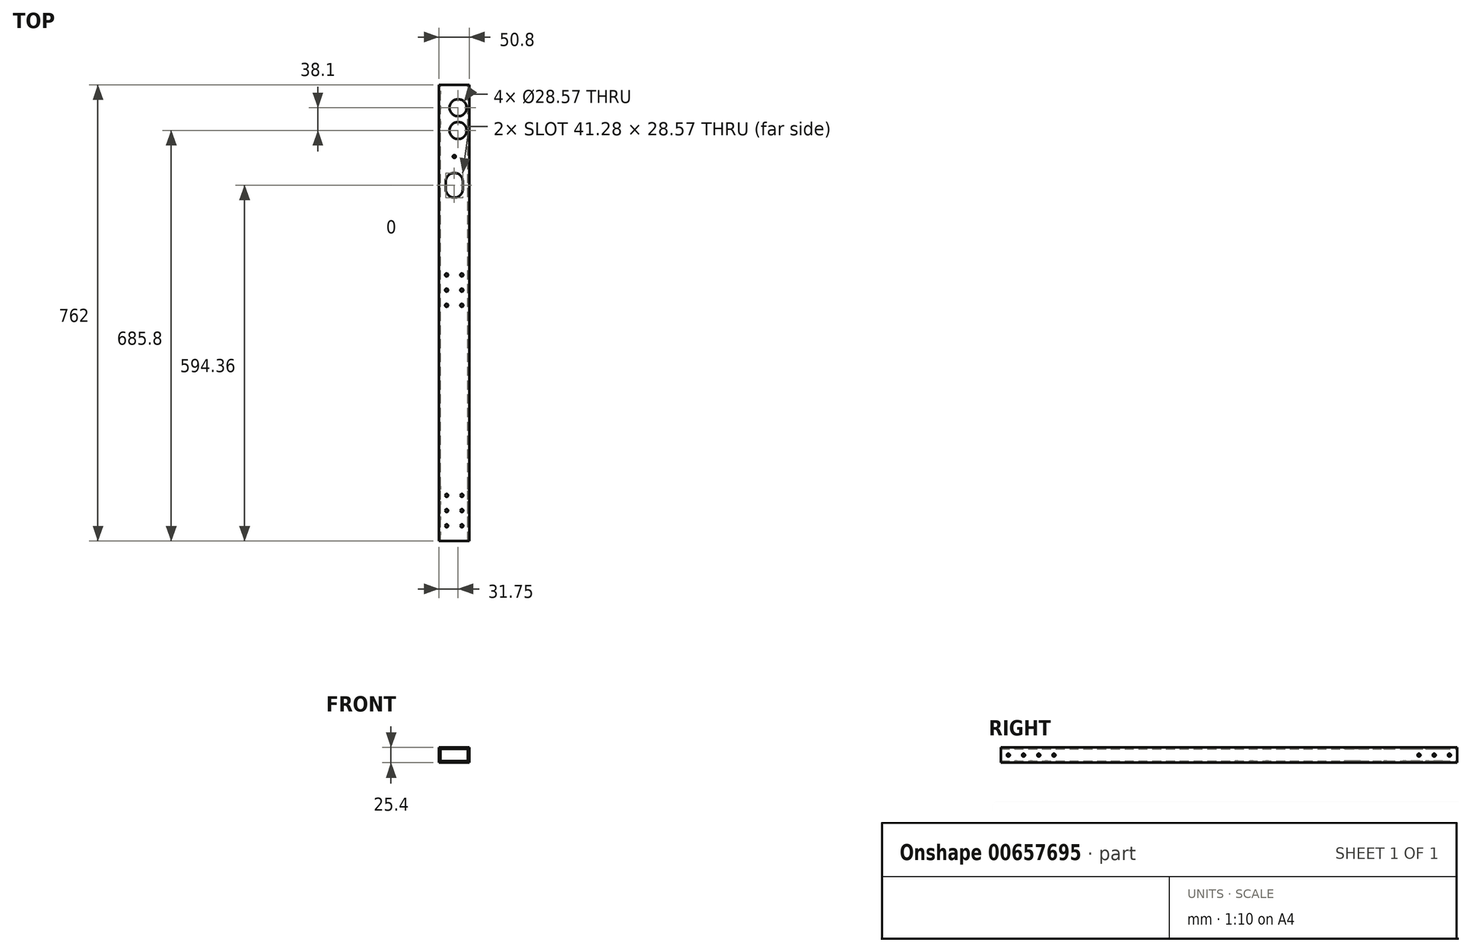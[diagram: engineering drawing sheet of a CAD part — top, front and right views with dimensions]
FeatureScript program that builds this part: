
annotation { "Feature Type Name" : "Feature", "Feature Type Description" : "" }
export const myFeature = defineFeature(function(context is Context, id is Id, definition is map)
    precondition{}
    {
        {
            var Q0;
            Q0=qCreatedBy(makeId("Front.planeOp"),FACE);
            var sketch = newSketch(context, id + "F0", { "sketchPlane" : qUnion([Q0])});
            skLineSegment(sketch, "E0.bottom", {"start": v(0, 0) * mm, "end": v(50.8, 0) * mm});
            skLineSegment(sketch, "E0.top", {"start": v(0, 25.4) * mm, "end": v(50.8, 25.4) * mm});
            skLineSegment(sketch, "E0.left", {"start": v(0, 0) * mm, "end": v(0, 25.4) * mm});
            skLineSegment(sketch, "E0.right", {"start": v(50.8, 0) * mm, "end": v(50.8, 25.4) * mm});
            skLineSegment(sketch, "E1.bottom", {"start": v(2.54, 22.86) * mm, "end": v(48.26, 22.86) * mm});
            skLineSegment(sketch, "E1.top", {"start": v(2.54, 2.54) * mm, "end": v(48.26, 2.54) * mm});
            skLineSegment(sketch, "E1.left", {"start": v(2.54, 22.86) * mm, "end": v(2.54, 2.54) * mm});
            skLineSegment(sketch, "E1.right", {"start": v(48.26, 22.86) * mm, "end": v(48.26, 2.54) * mm});
            skSolve(sketch);
        }
        {
            var Q0;
            Q0=makeQuery(id+"F0.imprint","IMPRINT",FACE,{"disambiguationData":[TD([[makeQuery(id+"F0.imprint","IMPRINT",EDGE,{"derivedFrom":sQuery(id+"F0.wireOp",EDGE,"E0.bottom")}),1.0]])]});
            extrude(context, id + "F1", {"entities" : qUnion([Q0]), "depth" : 787.4 * mm, "offsetDistance" : 25.4 * mm});
        }
        {
            var Q0;
            Q0=makeQuery(id+"F1.opExtrude","SWEPT_FACE",FACE,{"disambiguationData":[OSD([sQuery(id+"F0.wireOp",EDGE,"E0.right")])]});
            var sketch = newSketch(context, id + "F2", { "sketchPlane" : qUnion([Q0])});
            skLineSegment(sketch, "E2", {"start": v(0, 12.7) * mm, "end": v(-787.4, 12.7) * mm, "construction": true});
            skCircle(sketch, "E3", {"center": v(-12.7, 12.7) * mm, "radius": 2.55 * mm});
            skCircle(sketch, "E4", {"center": v(-38.1, 12.7) * mm, "radius": 2.55 * mm});
            skCircle(sketch, "E5", {"center": v(-63.5, 12.7) * mm, "radius": 2.55 * mm});
            skCircle(sketch, "E6", {"center": v(-88.9, 12.7) * mm, "radius": 2.55 * mm});
            skCircle(sketch, "E7", {"center": v(-774.7, 12.7) * mm, "radius": 2.55 * mm});
            skCircle(sketch, "E8", {"center": v(-749.3, 12.7) * mm, "radius": 2.55 * mm});
            skCircle(sketch, "E9", {"center": v(-723.9, 12.7) * mm, "radius": 2.55 * mm});
            skCircle(sketch, "E10", {"center": v(-698.5, 12.7) * mm, "radius": 2.55 * mm});
            skSolve(sketch);
        }
        {
            var Q0;
            Q0=makeQuery(id+"F1.opExtrude","SWEPT_FACE",FACE,{"disambiguationData":[OSD([sQuery(id+"F0.wireOp",EDGE,"E0.top")])]});
            var sketch = newSketch(context, id + "F3", { "sketchPlane" : qUnion([Q0])});
            skCircle(sketch, "E11", {"center": v(31.75, -63.5) * mm, "radius": 14.29 * mm});
            skCircle(sketch, "E12", {"center": v(25.4, -186.7) * mm, "radius": 14.29 * mm});
            skCircle(sketch, "E13", {"center": v(25.4, -199.39) * mm, "radius": 14.29 * mm});
            skCircle(sketch, "E14", {"center": v(12.7, -736.6) * mm, "radius": 2.49 * mm});
            skCircle(sketch, "E15.0.1.0", {"center": v(12.7, -711.2) * mm, "radius": 2.49 * mm});
            skCircle(sketch, "E15.1.0.0", {"center": v(38.1, -736.6) * mm, "radius": 2.49 * mm});
            skCircle(sketch, "E15.1.1.0", {"center": v(38.1, -711.2) * mm, "radius": 2.49 * mm});
            skLineSegment(sketch, "E15.direction1", {"start": v(12.7, -736.6) * mm, "end": v(38.1, -736.6) * mm, "construction": true});
            skLineSegment(sketch, "E15.direction2", {"start": v(12.7, -736.6) * mm, "end": v(12.7, -711.2) * mm, "construction": true});
            skCircle(sketch, "E16", {"center": v(12.7, -342.9) * mm, "radius": 2.55 * mm});
            skPoint(sketch, "E17", {"position": v(0, -341.39) * mm});
            skCircle(sketch, "E18.0.1.0", {"center": v(12.7, -368.3) * mm, "radius": 2.55 * mm});
            skCircle(sketch, "E18.0.2.0", {"center": v(12.7, -393.7) * mm, "radius": 2.55 * mm});
            skCircle(sketch, "E18.1.0.0", {"center": v(38.1, -342.9) * mm, "radius": 2.55 * mm});
            skCircle(sketch, "E18.1.1.0", {"center": v(38.1, -368.3) * mm, "radius": 2.55 * mm});
            skCircle(sketch, "E18.1.2.0", {"center": v(38.1, -393.7) * mm, "radius": 2.55 * mm});
            skLineSegment(sketch, "E18.direction1", {"start": v(12.7, -342.9) * mm, "end": v(38.1, -342.9) * mm, "construction": true});
            skLineSegment(sketch, "E18.direction2", {"start": v(12.7, -342.9) * mm, "end": v(12.7, -368.3) * mm, "construction": true});
            skLineSegment(sketch, "E19", {"start": v(39.69, -186.7) * mm, "end": v(39.69, -199.39) * mm});
            skLineSegment(sketch, "E20", {"start": v(11.11, -186.7) * mm, "end": v(11.11, -199.39) * mm});
            skCircle(sketch, "E21", {"center": v(25.4, -145.03) * mm, "radius": 2.49 * mm});
            skCircle(sketch, "E22", {"center": v(38.1, -762) * mm, "radius": 2.49 * mm});
            skCircle(sketch, "E23", {"center": v(12.7, -762) * mm, "radius": 2.49 * mm});
            skLineSegment(sketch, "E24.bottom", {"start": v(0, 0) * mm, "end": v(50.8, 0) * mm});
            skLineSegment(sketch, "E24.top", {"start": v(0, -25.4) * mm, "end": v(50.8, -25.4) * mm});
            skLineSegment(sketch, "E24.left", {"start": v(0, 0) * mm, "end": v(0, -25.4) * mm});
            skLineSegment(sketch, "E24.right", {"start": v(50.8, 0) * mm, "end": v(50.8, -25.4) * mm});
            skCircle(sketch, "E25", {"center": v(31.75, -101.6) * mm, "radius": 14.29 * mm});
            skSolve(sketch);
        }
        {
            var Q0;
            Q0=makeQuery(id+"F3.imprint","IMPRINT",FACE,{"disambiguationData":[TD([[makeQuery(id+"F3.imprint","IMPRINT",EDGE,{"derivedFrom":sQuery(id+"F3.wireOp",EDGE,"E11")}),1.0]])]});
            var Q1;
            Q1=makeQuery(id+"F3.imprint","IMPRINT",FACE,{"disambiguationData":[TD([[makeQuery(id+"F3.imprint","IMPRINT",EDGE,{"derivedFrom":sQuery(id+"F3.wireOp",EDGE,"uvUDpf29-BH4l-E19a-3uxY-FCehscGXEqBA")}),1.0]])]});
            var Q2;
            Q2=makeQuery(id+"F3.imprint","IMPRINT",FACE,{"disambiguationData":[TD([[makeQuery(id+"F3.imprint","IMPRINT",EDGE,{"derivedFrom":sQuery(id+"F3.wireOp",EDGE,"E14")}),1.0]])]});
            var Q3;
            Q3=makeQuery(id+"F3.imprint","IMPRINT",FACE,{"disambiguationData":[TD([[makeQuery(id+"F3.imprint","IMPRINT",EDGE,{"derivedFrom":sQuery(id+"F3.wireOp",EDGE,"E15.1.0.0")}),1.0]])]});
            var Q4;
            Q4=makeQuery(id+"F3.imprint","IMPRINT",FACE,{"disambiguationData":[TD([[makeQuery(id+"F3.imprint","IMPRINT",EDGE,{"derivedFrom":sQuery(id+"F3.wireOp",EDGE,"E15.0.1.0")}),1.0]])]});
            var Q5;
            Q5=makeQuery(id+"F3.imprint","IMPRINT",FACE,{"disambiguationData":[TD([[makeQuery(id+"F3.imprint","IMPRINT",EDGE,{"derivedFrom":sQuery(id+"F3.wireOp",EDGE,"E15.1.1.0")}),1.0]])]});
            var Q6;
            Q6=makeQuery(id+"F3.imprint","IMPRINT",FACE,{"disambiguationData":[TD([[makeQuery(id+"F3.imprint","IMPRINT",EDGE,{"derivedFrom":sQuery(id+"F3.wireOp",EDGE,"E18.1.2.0")}),1.0]])]});
            var Q7;
            Q7=makeQuery(id+"F3.imprint","IMPRINT",FACE,{"disambiguationData":[TD([[makeQuery(id+"F3.imprint","IMPRINT",EDGE,{"derivedFrom":sQuery(id+"F3.wireOp",EDGE,"E18.1.1.0")}),1.0]])]});
            var Q8;
            Q8=makeQuery(id+"F3.imprint","IMPRINT",FACE,{"disambiguationData":[TD([[makeQuery(id+"F3.imprint","IMPRINT",EDGE,{"derivedFrom":sQuery(id+"F3.wireOp",EDGE,"E16")}),1.0]])]});
            var Q9;
            Q9=makeQuery(id+"F3.imprint","IMPRINT",FACE,{"disambiguationData":[TD([[makeQuery(id+"F3.imprint","IMPRINT",EDGE,{"derivedFrom":sQuery(id+"F3.wireOp",EDGE,"E18.1.0.0")}),1.0]])]});
            var Q10;
            Q10=makeQuery(id+"F3.imprint","IMPRINT",FACE,{"disambiguationData":[TD([[makeQuery(id+"F3.imprint","IMPRINT",EDGE,{"derivedFrom":sQuery(id+"F3.wireOp",EDGE,"E18.0.1.0")}),1.0]])]});
            var Q11;
            Q11=makeQuery(id+"F3.imprint","IMPRINT",FACE,{"disambiguationData":[TD([[makeQuery(id+"F3.imprint","IMPRINT",EDGE,{"derivedFrom":sQuery(id+"F3.wireOp",EDGE,"E18.0.2.0")}),1.0]])]});
            var Q12;
            {var subQ0=sQuery(id+"F3.wireOp",EDGE,"E12");var subQ1=makeQuery(id+"F3.imprint","INTERSECT",VERTEX,{"derivedFrom":[subQ0,sQuery(id+"F3.wireOp",EDGE,"5gnyUQr0-5ffU-JKi1-1kLP-EUn8UOzYsjTT")]});Q12=makeQuery(id+"F3.imprint","IMPRINT",FACE,{"disambiguationData":[TD([[makeQuery(id+"F3.imprint","IMPRINT",EDGE,{"disambiguationData":[TD([[subQ1,1.0]])],"derivedFrom":subQ0}),1.0]])]});}
            var Q13;
            {var subQ0=sQuery(id+"F3.wireOp",EDGE,"5gnyUQr0-5ffU-JKi1-1kLP-EUn8UOzYsjTT");Q13=makeQuery(id+"F3.imprint","IMPRINT",FACE,{"disambiguationData":[TD([[makeQuery(id+"F3.imprint","IMPRINT",EDGE,{"derivedFrom":subQ0}),-1.0]])]});}
            var Q14;
            {var subQ0=sQuery(id+"F3.wireOp",EDGE,"77zC9NZe-G8aT-6EGM-fQsp-HiLRZIQ0p5GJ");Q14=makeQuery(id+"F3.imprint","IMPRINT",FACE,{"disambiguationData":[TD([[makeQuery(id+"F3.imprint","IMPRINT",EDGE,{"derivedFrom":subQ0}),1.0]])]});}
            var Q15;
            {var subQ0=sQuery(id+"F3.wireOp",EDGE,"77zC9NZe-G8aT-6EGM-fQsp-HiLRZIQ0p5GJ");Q15=makeQuery(id+"F3.imprint","IMPRINT",FACE,{"disambiguationData":[TD([[makeQuery(id+"F3.imprint","IMPRINT",EDGE,{"derivedFrom":subQ0}),-1.0]])]});}
            var Q16;
            Q16=makeQuery(id+"F3.imprint","IMPRINT",FACE,{"disambiguationData":[TD([[makeQuery(id+"F3.imprint","IMPRINT",EDGE,{"derivedFrom":sQuery(id+"F3.wireOp",EDGE,"E21")}),1.0]])]});
            var Q17;
            {var subQ0=sQuery(id+"F3.wireOp",EDGE,"E13");var subQ1=sQuery(id+"F3.wireOp",EDGE,"E12");var subQ2=makeQuery(id+"F3.imprint","INTERSECT",VERTEX,{"disambiguationData":[OD(0.0)],"derivedFrom":[subQ1,subQ0]});Q17=makeQuery(id+"F3.imprint","IMPRINT",FACE,{"disambiguationData":[TD([[makeQuery(id+"F3.imprint","IMPRINT",EDGE,{"disambiguationData":[TD([[subQ2,-1.0]])],"derivedFrom":subQ1}),1.0]])]});}
            var Q18;
            {var subQ0=sQuery(id+"F3.wireOp",EDGE,"E13");var subQ1=sQuery(id+"F3.wireOp",EDGE,"E12");var subQ2=makeQuery(id+"F3.imprint","INTERSECT",VERTEX,{"disambiguationData":[OD(0.0)],"derivedFrom":[subQ1,subQ0]});Q18=makeQuery(id+"F3.imprint","IMPRINT",FACE,{"disambiguationData":[TD([[makeQuery(id+"F3.imprint","IMPRINT",EDGE,{"disambiguationData":[TD([[subQ2,-1.0]])],"derivedFrom":subQ1}),-1.0]])]});}
            var Q19;
            {var subQ0=sQuery(id+"F3.wireOp",EDGE,"E20");Q19=makeQuery(id+"F3.imprint","IMPRINT",FACE,{"disambiguationData":[TD([[makeQuery(id+"F3.imprint","IMPRINT",EDGE,{"derivedFrom":subQ0}),1.0]])]});}
            var Q20;
            {var subQ0=sQuery(id+"F3.wireOp",EDGE,"E19");Q20=makeQuery(id+"F3.imprint","IMPRINT",FACE,{"disambiguationData":[TD([[makeQuery(id+"F3.imprint","IMPRINT",EDGE,{"derivedFrom":subQ0}),-1.0]])]});}
            var Q21;
            Q21=makeQuery(id+"F3.imprint","IMPRINT",FACE,{"disambiguationData":[TD([[makeQuery(id+"F3.imprint","IMPRINT",EDGE,{"derivedFrom":sQuery(id+"F3.wireOp",EDGE,"E22")}),1.0]])]});
            var Q22;
            Q22=makeQuery(id+"F3.imprint","IMPRINT",FACE,{"disambiguationData":[TD([[makeQuery(id+"F3.imprint","IMPRINT",EDGE,{"derivedFrom":sQuery(id+"F3.wireOp",EDGE,"E23")}),1.0]])]});
            var Q23;
            Q23=makeQuery(id+"F3.imprint","IMPRINT",FACE,{"disambiguationData":[TD([[makeQuery(id+"F3.imprint","IMPRINT",EDGE,{"derivedFrom":sQuery(id+"F3.wireOp",EDGE,"E25")}),1.0]])]});
            extrude(context, id + "F4", {"entities" : qUnion([Q0, Q1, Q2, Q3, Q4, Q5, Q6, Q7, Q8, Q9, Q10, Q11, Q12, Q13, Q14, Q15, Q16, Q17, Q18, Q19, Q20, Q21, Q22, Q23]), "operationType" : NewBodyOperationType.REMOVE, "oppositeDirection" : true, "depth" : 25.4 * mm, "offsetDistance" : 25.4 * mm});
        }
        {
            var Q0;
            Q0 = qSketchRegion(id + "F2", true);
            extrude(context, id + "F5", {"entities" : qUnion([Q0]), "operationType" : NewBodyOperationType.REMOVE, "endBound" : BoundingType.THROUGH_ALL, "oppositeDirection" : true, "depth" : 25.4 * mm, "offsetDistance" : 25.4 * mm});
        }
        {
            var Q0;
            Q0 = qSketchRegion(id + "F0", true);
            extrude(context, id + "F6", {"entities" : qUnion([Q0]), "operationType" : NewBodyOperationType.REMOVE, "depth" : 25.4 * mm, "offsetDistance" : 25.4 * mm});
        }
    });
